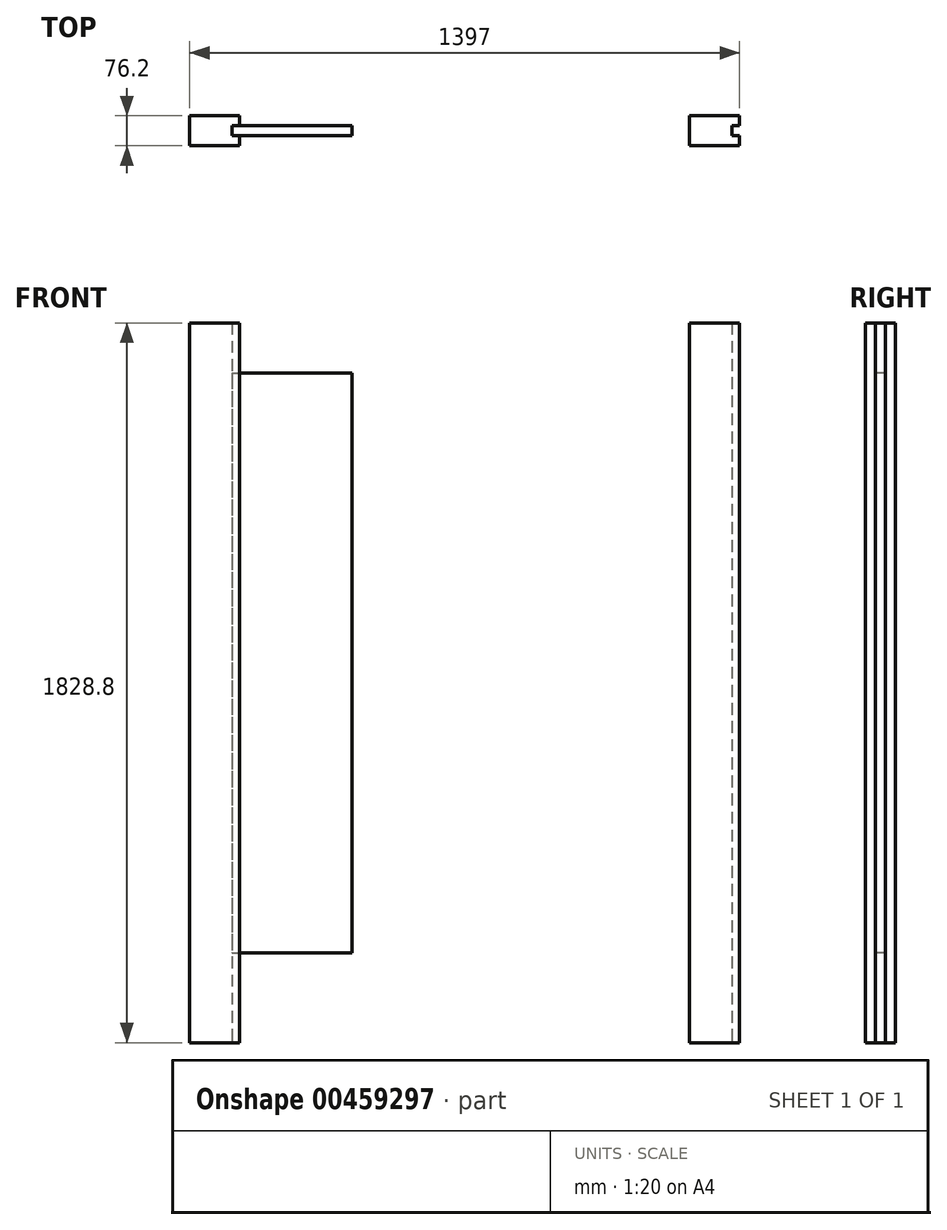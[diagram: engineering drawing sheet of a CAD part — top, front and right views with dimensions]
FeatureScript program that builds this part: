
annotation { "Feature Type Name" : "Feature", "Feature Type Description" : "" }
export const myFeature = defineFeature(function(context is Context, id is Id, definition is map)
    precondition{}
    {
        {
            var Q0;
            Q0=qCreatedBy(makeId("Top.planeOp"),FACE);
            var sketch = newSketch(context, id + "F0", { "sketchPlane" : qUnion([Q0])});
            skLineSegment(sketch, "E0.bottom", {"start": v(-80.92, 38.1) * mm, "end": v(46.08, 38.1) * mm});
            skLineSegment(sketch, "E0.top", {"start": v(-80.92, -38.1) * mm, "end": v(46.08, -38.1) * mm});
            skLineSegment(sketch, "E0.left", {"start": v(-80.92, 38.1) * mm, "end": v(-80.92, -38.1) * mm});
            skLineSegment(sketch, "E1.bottom", {"start": v(46.08, 12.7) * mm, "end": v(27.03, 12.7) * mm});
            skLineSegment(sketch, "E1.top", {"start": v(46.08, -12.7) * mm, "end": v(27.03, -12.7) * mm});
            skLineSegment(sketch, "E1.right", {"start": v(27.03, 12.7) * mm, "end": v(27.03, -12.7) * mm});
            skLineSegment(sketch, "E2", {"start": v(46.08, 38.1) * mm, "end": v(46.08, 12.7) * mm});
            skLineSegment(sketch, "E3", {"start": v(46.08, -12.7) * mm, "end": v(46.08, -38.1) * mm});
            skSolve(sketch);
        }
        {
            var Q0;
            Q0 = qSketchRegion(id + "F0", true);
            extrude(context, id + "F1", {"entities" : qUnion([Q0]), "depth" : 1828.8 * mm});
        }
        {
            var Q0;
            Q0=qCreatedBy(makeId("Top.planeOp"),FACE);
            cPlane(context, id + "F2", {"entities" : qUnion([Q0]), "cplaneType" : CPlaneType.OFFSET, "offset" : 228.6 * mm, "width" : 152.4 * mm, "height" : 152.4 * mm});
        }
        {
            var Q0;
            Q0=qCreatedBy(id+"F2.planeOp",FACE);
            var sketch = newSketch(context, id + "F3", { "sketchPlane" : qUnion([Q0])});
            skLineSegment(sketch, "E4.bottom", {"start": v(27.03, 12.7) * mm, "end": v(179.43, 12.7) * mm});
            skLineSegment(sketch, "E4.top", {"start": v(27.03, -12.7) * mm, "end": v(179.43, -12.7) * mm});
            skLineSegment(sketch, "E4.left", {"start": v(27.03, 12.7) * mm, "end": v(27.03, -12.7) * mm});
            skLineSegment(sketch, "E4.right", {"start": v(179.43, 12.7) * mm, "end": v(179.43, -12.7) * mm});
            skSolve(sketch);
        }
        {
            var Q0;
            Q0 = qSketchRegion(id + "F3", true);
            extrude(context, id + "F4", {"entities" : qUnion([Q0]), "depth" : 1473.2 * mm});
        }
        {
            var Q0;
            Q0=makeQuery(id+"F1.opExtrude","SWEPT_BODY",BODY,{"disambiguationData":[OSD([sQuery(id+"F0.wireOp",EDGE,"E0.bottom"),sQuery(id+"F0.wireOp",EDGE,"E0.top"),sQuery(id+"F0.wireOp",EDGE,"E0.left"),sQuery(id+"F0.wireOp",EDGE,"E1.bottom"),sQuery(id+"F0.wireOp",EDGE,"E1.top"),sQuery(id+"F0.wireOp",EDGE,"E1.right"),sQuery(id+"F0.wireOp",EDGE,"E2"),sQuery(id+"F0.wireOp",EDGE,"E3")])]});
            transform(context, id + "F5", {"entities" : qUnion([Q0]), "transformType" : TransformType.TRANSLATION_3D, "dx" : 1270 * mm, "dy" : 0 * mm, "dz" : 0 * mm, "makeCopy" : true});
        }
        {
            var Q0;
            Q0=makeQuery(id+"F4.opExtrude","CAP_FACE",FACE,{"disambiguationData":[OSD([sQuery(id+"F3.wireOp",EDGE,"E4.bottom"),sQuery(id+"F3.wireOp",EDGE,"E4.top"),sQuery(id+"F3.wireOp",EDGE,"E4.left"),sQuery(id+"F3.wireOp",EDGE,"E4.right")])],"isStart":false});
            var sketch = newSketch(context, id + "F6", { "sketchPlane" : qUnion([Q0])});
            skLineSegment(sketch, "E5.bottom", {"start": v(179.43, 6.35) * mm, "end": v(160.38, 6.35) * mm});
            skLineSegment(sketch, "E5.top", {"start": v(179.43, -6.35) * mm, "end": v(160.38, -6.35) * mm});
            skLineSegment(sketch, "E5.left", {"start": v(179.43, -6.35) * mm, "end": v(179.43, 6.35) * mm});
            skLineSegment(sketch, "E5.right", {"start": v(160.38, -6.35) * mm, "end": v(160.38, 6.35) * mm});
            skSolve(sketch);
        }
        {
            var Q0;
            Q0 = qSketchRegion(id + "F6", true);
            extrude(context, id + "F7", {"entities" : qUnion([Q0]), "operationType" : NewBodyOperationType.REMOVE, "oppositeDirection" : true, "depth" : 2540 * mm});
        }
        {
            var Q0;
            Q0=qCreatedBy(id+"F2.planeOp",FACE);
            var sketch = newSketch(context, id + "F8", { "sketchPlane" : qUnion([Q0])});
            skLineSegment(sketch, "E6.bottom", {"start": v(160.38, 6.35) * mm, "end": v(179.43, 6.35) * mm});
            skLineSegment(sketch, "E6.top", {"start": v(160.38, -6.35) * mm, "end": v(179.43, -6.35) * mm});
            skLineSegment(sketch, "E6.left", {"start": v(160.38, 6.35) * mm, "end": v(160.38, -6.35) * mm});
            skLineSegment(sketch, "E7.bottom", {"start": v(179.43, 12.7) * mm, "end": v(331.83, 12.7) * mm});
            skLineSegment(sketch, "E7.top", {"start": v(179.43, -12.7) * mm, "end": v(331.83, -12.7) * mm});
            skLineSegment(sketch, "E7.right", {"start": v(331.83, 12.7) * mm, "end": v(331.83, -12.7) * mm});
            skLineSegment(sketch, "E8", {"start": v(179.43, 12.7) * mm, "end": v(179.43, 6.35) * mm});
            skLineSegment(sketch, "E9", {"start": v(179.43, -6.35) * mm, "end": v(179.43, -12.7) * mm});
            skSolve(sketch);
        }
        {
            var Q0;
            Q0 = qSketchRegion(id + "F8", true);
            extrude(context, id + "F9", {"entities" : qUnion([Q0]), "operationType" : NewBodyOperationType.ADD, "depth" : 1473.2 * mm});
        }
    });
